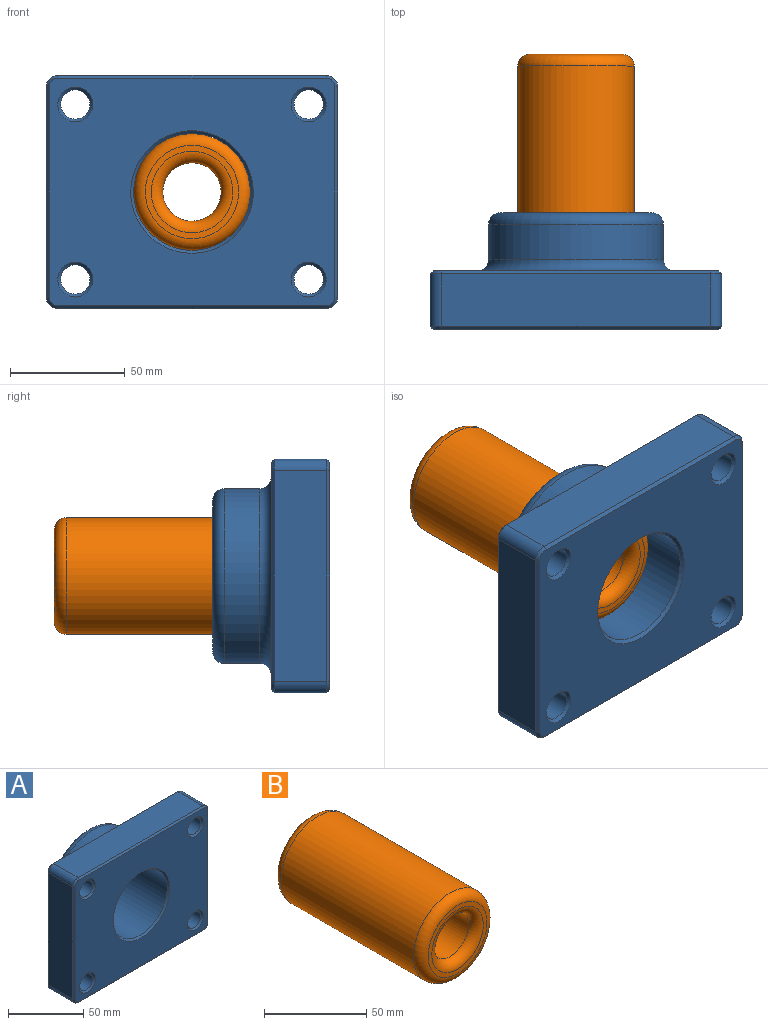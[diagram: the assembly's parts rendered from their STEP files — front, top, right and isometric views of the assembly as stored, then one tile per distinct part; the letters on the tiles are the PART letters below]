
ASSEMBLY  parts=2 mates=1
PART A: 45 faces, bbox 127x50.8x101.6 mm
  f0: plane 91.44x22.86mm, normal (-1,0,0), area 2090.3mm2, adj f11,f14,f20,f33
  f1: plane 116.84x22.86mm, normal (0,0,-1), area 2671mm2, adj f11,f12,f24,f32
  f2: plane 91.44x22.86mm, normal (1,0,0), area 2090.3mm2, adj f12,f13,f25,f28
  f3: plane 116.84x22.86mm, normal (0,0,1), area 2671mm2, adj f13,f14,f21,f29
  f4: cylinder r=6.35mm len=22.86mm, axis (0,1,0), area 912.1mm2, adj f37,f43
  f5: cylinder r=6.35mm len=22.86mm, axis (0,1,0), area 912.1mm2, adj f38,f40
  f6: cylinder r=6.35mm len=22.86mm, axis (0,1,0), area 912.1mm2, adj f36,f42
  f7: cylinder r=6.35mm len=22.86mm, axis (0,1,0), area 912.1mm2, adj f39,f41
  f8: cylinder r=25.41mm len=50.81mm, axis (0,1,0), area 7703.9mm2, adj f35,f44
  f9: plane 124.46x99.06mm, normal (0,-1,0), area 9351.2mm2, adj f19,f20,f21,f22,f23,f24,f25,f26
  f10: plane 124.46x99.06mm, normal (0,1,0), area 5729.3mm2, adj f17,f27,f28,f29,f30,f31,f32,f33
  f11: cylinder r=5.08mm len=22.86mm, axis (0,1,0), area 182.4mm2, adj f0,f1,f22,f34
  f12: cylinder r=5.08mm len=22.86mm, axis (0,-1,0), area 182.4mm2, adj f1,f2,f26,f30
  f13: cylinder r=5.08mm len=22.86mm, axis (0,1,0), area 182.4mm2, adj f2,f3,f23,f27
  f14: cylinder r=5.08mm len=22.86mm, axis (0,-1,0), area 182.4mm2, adj f0,f3,f19,f31
  f15: cylinder r=38.1mm len=76.2mm, axis (0,-1,0), area 3648.3mm2, adj f17,f18
  f16: plane 66.04x66.04mm, normal (0,1,0), area 1189.7mm2, adj f18,f35
  f17: torus R=43.18mm, axis (0,-1,0), area 2002.8mm2, adj f10,f15
  f18: torus R=33.02mm, axis (0,-1,0), area 1817.7mm2, adj f15,f16
  f19: cone r=3.81mm half-angle=45deg, axis (0,1,0), area 12.5mm2, adj f9,f14,f20,f21
  f20: plane 91.44x1.27mm, normal (-0.71,-0.71,0), area 164.2mm2, adj f0,f9,f19,f22
  f21: plane 116.84x1.27mm, normal (0,-0.71,0.71), area 209.9mm2, adj f3,f9,f19,f23
  f22: cone r=3.81mm half-angle=45deg, axis (0,1,0), area 12.5mm2, adj f9,f11,f20,f24
  f23: cone r=3.81mm half-angle=45deg, axis (0,1,0), area 12.5mm2, adj f9,f13,f21,f25
  f24: plane 116.84x1.27mm, normal (0,-0.71,-0.71), area 209.9mm2, adj f1,f9,f22,f26
  f25: plane 91.44x1.27mm, normal (0.71,-0.71,0), area 164.2mm2, adj f2,f9,f23,f26
  f26: cone r=3.81mm half-angle=45deg, axis (0,1,0), area 12.5mm2, adj f9,f12,f24,f25
  f27: cone r=3.81mm half-angle=45deg, axis (0,-1,0), area 12.5mm2, adj f10,f13,f28,f29
  f28: plane 91.44x1.27mm, normal (0.71,0.71,0), area 164.2mm2, adj f2,f10,f27,f30
  f29: plane 116.84x1.27mm, normal (0,0.71,0.71), area 209.9mm2, adj f3,f10,f27,f31
  f30: cone r=3.81mm half-angle=45deg, axis (0,-1,0), area 12.5mm2, adj f10,f12,f28,f32
  f31: cone r=3.81mm half-angle=45deg, axis (0,-1,0), area 12.5mm2, adj f10,f14,f29,f33
  f32: plane 116.84x1.27mm, normal (0,0.71,-0.71), area 209.9mm2, adj f1,f10,f30,f34
  f33: plane 91.44x1.27mm, normal (-0.71,0.71,0), area 164.2mm2, adj f0,f10,f31,f34
  f34: cone r=3.81mm half-angle=45deg, axis (0,-1,0), area 12.5mm2, adj f10,f11,f32,f33
  f35: cone r=26.68mm half-angle=45deg, axis (0,1,0), area 293.9mm2, adj f8,f16
  f36: cone r=7.62mm half-angle=45deg, axis (0,1,0), area 78.8mm2, adj f6,f10
  f37: cone r=7.62mm half-angle=45deg, axis (0,1,0), area 78.8mm2, adj f4,f10
  f38: cone r=7.62mm half-angle=45deg, axis (0,1,0), area 78.8mm2, adj f5,f10
  f39: cone r=7.62mm half-angle=45deg, axis (0,1,0), area 78.8mm2, adj f7,f10
  f40: cone r=6.35mm half-angle=45deg, axis (0,-1,0), area 78.8mm2, adj f5,f9
  f41: cone r=6.35mm half-angle=45deg, axis (0,-1,0), area 78.8mm2, adj f7,f9
  f42: cone r=6.35mm half-angle=45deg, axis (0,-1,0), area 78.8mm2, adj f6,f9
  f43: cone r=6.35mm half-angle=45deg, axis (0,-1,0), area 78.8mm2, adj f4,f9
  f44: cone r=25.41mm half-angle=45deg, axis (0,-1,0), area 293.9mm2, adj f8,f9
PART B: 8 faces, bbox 55x101.6x55 mm
  f0: cylinder r=12.7mm len=91.44mm, axis (0,1,0), area 7296.6mm2, adj f4,f6
  f1: cylinder r=25.4mm len=91.44mm, axis (0,1,0), area 14593.2mm2, adj f5,f7
  f2: plane 40.64x40.64mm, normal (0,-1,0), area 304mm2, adj f6,f7
  f3: plane 40.64x40.64mm, normal (0,1,0), area 304mm2, adj f4,f5
  f4: torus R=17.78mm, axis (0,-1,0), area 729.3mm2, adj f0,f3
  f5: torus R=20.32mm, axis (0,-1,0), area 1180.9mm2, adj f1,f3
  f6: torus R=17.78mm, axis (0,-1,0), area 729.3mm2, adj f0,f2
  f7: torus R=20.32mm, axis (0,-1,0), area 1180.9mm2, adj f1,f2
PLACE A at identity fixed
PLACE B rot(axis=(0,1,0),76.5deg) t=(0,94.39,0)mm
MATE cylindrical A.f8 <-> B.f1  axis (0,1,0) through (0,-12.7,0)mm
